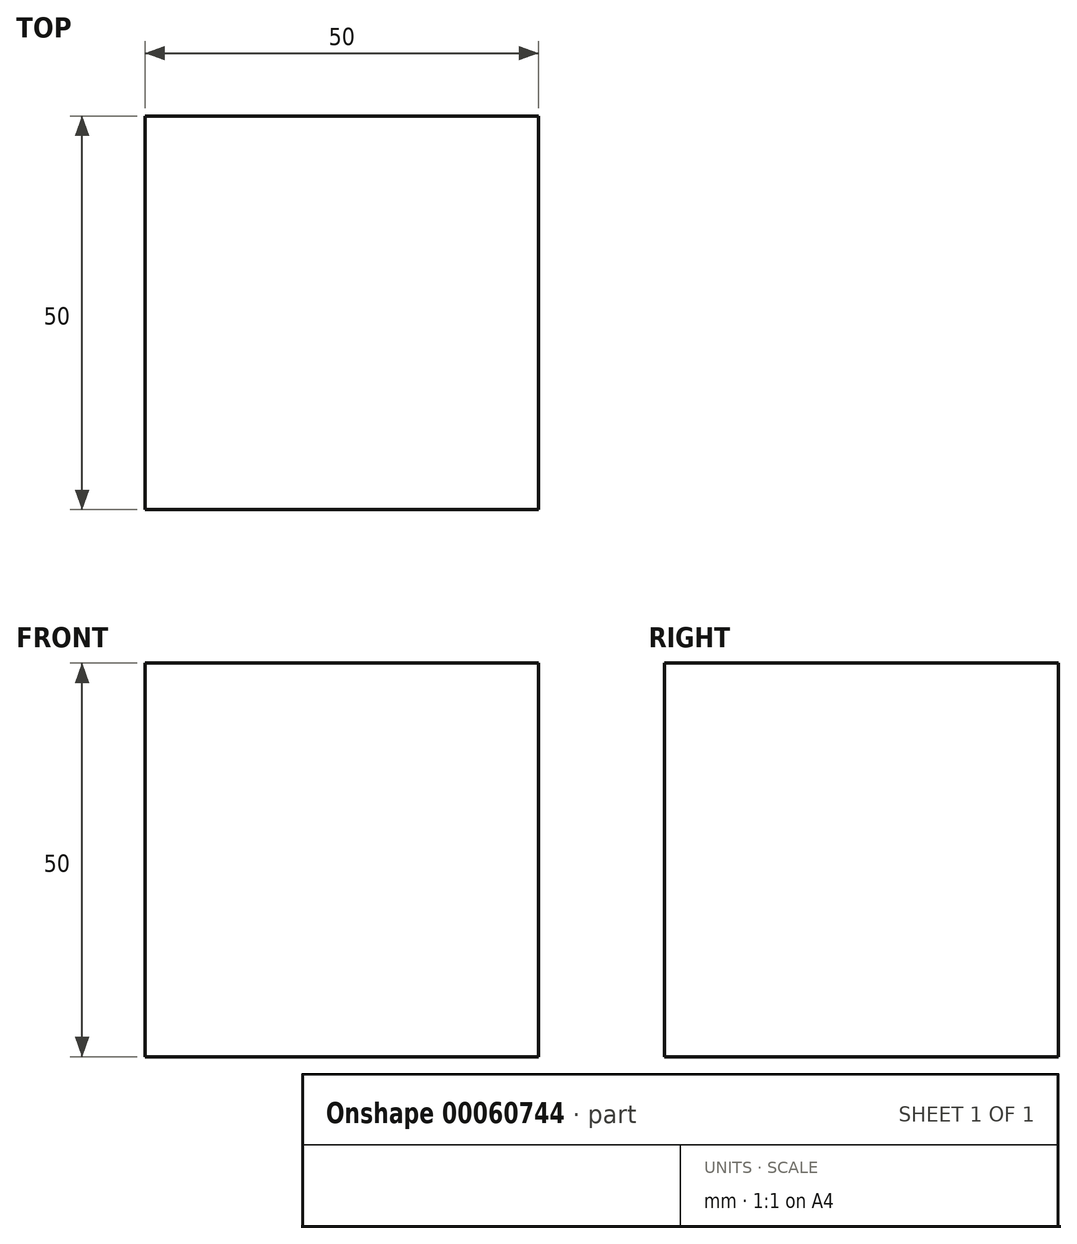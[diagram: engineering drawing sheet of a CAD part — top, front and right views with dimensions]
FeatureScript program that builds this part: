
annotation { "Feature Type Name" : "Feature", "Feature Type Description" : "" }
export const myFeature = defineFeature(function(context is Context, id is Id, definition is map)
    precondition{}
    {
        {
            var Q0;
            Q0=qCreatedBy(makeId("Top.planeOp"),FACE);
            var sketch = newSketch(context, id + "F0", { "sketchPlane" : qUnion([Q0])});
            skLineSegment(sketch, "E0.bottom", {"start": v(0, 0) * mm, "end": v(50, 0) * mm});
            skLineSegment(sketch, "E0.top", {"start": v(0, 50) * mm, "end": v(50, 50) * mm});
            skLineSegment(sketch, "E0.left", {"start": v(0, 0) * mm, "end": v(0, 50) * mm});
            skLineSegment(sketch, "E0.right", {"start": v(50, 0) * mm, "end": v(50, 50) * mm});
            skSolve(sketch);
        }
        {
            var Q0;
            Q0=makeQuery(id+"F0.imprint","IMPRINT",FACE,{"disambiguationData":[TD([[makeQuery(id+"F0.imprint","IMPRINT",EDGE,{"derivedFrom":sQuery(id+"F0.wireOp",EDGE,"E0.bottom")}),1.0]])]});
            extrude(context, id + "F1", {"entities" : qUnion([Q0]), "depth" : 50 * mm});
        }
    });
